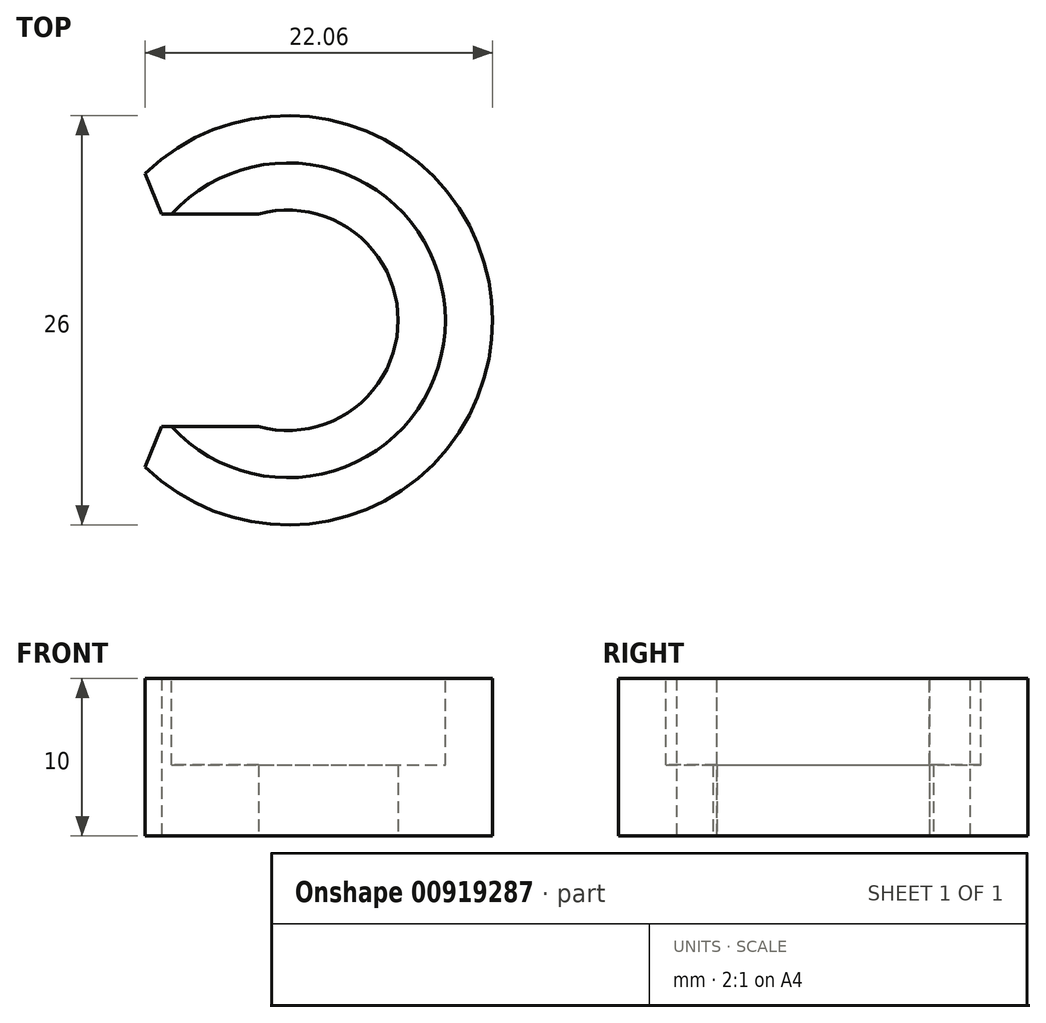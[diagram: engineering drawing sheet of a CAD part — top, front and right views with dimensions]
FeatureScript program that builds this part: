
annotation { "Feature Type Name" : "Feature", "Feature Type Description" : "" }
export const myFeature = defineFeature(function(context is Context, id is Id, definition is map)
    precondition{}
    {
        {
            var Q0;
            Q0=qCreatedBy(makeId("Top.planeOp"),FACE);
            var sketch = newSketch(context, id + "F0", { "sketchPlane" : qUnion([Q0])});
            skCircle(sketch, "E0", {"center": v(0, 0) * mm, "radius": 13 * mm});
            skCircle(sketch, "E1", {"center": v(0, 0) * mm, "radius": 7 * mm});
            skSolve(sketch);
        }
        {
            var Q0;
            Q0 = qSketchRegion(id + "F0", true);
            extrude(context, id + "F1", {"entities" : qUnion([Q0]), "depth" : 10 * mm, "offsetDistance" : 25 * mm});
        }
        {
            var Q0;
            Q0=makeQuery(id+"F1.opExtrude","CAP_FACE",FACE,{"disambiguationData":[OSD([sQuery(id+"F0.wireOp",EDGE,"E0"),sQuery(id+"F0.wireOp",EDGE,"E1")])],"isStart":false});
            var sketch = newSketch(context, id + "F2", { "sketchPlane" : qUnion([Q0])});
            skCircle(sketch, "E2", {"center": v(0, 0) * mm, "radius": 10 * mm});
            skSolve(sketch);
        }
        {
            var Q0;
            Q0=makeQuery(id+"F2.imprint","IMPRINT",FACE,{"disambiguationData":[TD([[makeQuery(id+"F2.imprint","IMPRINT",EDGE,{"derivedFrom":sQuery(id+"F2.wireOp",EDGE,"E2")}),1.0]])]});
            extrude(context, id + "F3", {"entities" : qUnion([Q0]), "operationType" : NewBodyOperationType.REMOVE, "oppositeDirection" : true, "depth" : 5.5 * mm, "offsetDistance" : 25 * mm});
        }
        {
            var Q0;
            Q0=makeQuery(id+"F1.opExtrude","CAP_FACE",FACE,{"disambiguationData":[OSD([sQuery(id+"F0.wireOp",EDGE,"E0"),sQuery(id+"F0.wireOp",EDGE,"E1")])],"isStart":false});
            var sketch = newSketch(context, id + "F4", { "sketchPlane" : qUnion([Q0])});
            skLineSegment(sketch, "E3.bottom", {"start": v(0, 6.75) * mm, "end": v(-13.5, 6.75) * mm});
            skLineSegment(sketch, "E3.top", {"start": v(0, -6.75) * mm, "end": v(-13.5, -6.75) * mm});
            skLineSegment(sketch, "E3.left", {"start": v(0, 6.75) * mm, "end": v(0, -6.75) * mm});
            skLineSegment(sketch, "E3.right", {"start": v(-13.5, 6.75) * mm, "end": v(-13.5, -6.75) * mm});
            skSolve(sketch);
        }
        {
            var Q0;
            Q0 = qSketchRegion(id + "F4", true);
            extrude(context, id + "F5", {"entities" : qUnion([Q0]), "operationType" : NewBodyOperationType.REMOVE, "endBound" : BoundingType.THROUGH_ALL, "oppositeDirection" : true, "depth" : 25 * mm, "offsetDistance" : 25 * mm});
        }
        {
            var Q0;
            Q0=makeQuery(id+"F5.boolean.opBoolean","INTERSECT",EDGE,{"derivedFrom":[makeQuery(id+"F1.opExtrude","SWEPT_FACE",FACE,{"disambiguationData":[OSD([sQuery(id+"F0.wireOp",EDGE,"E0")])]}),makeQuery(id+"F5.opExtrude","SWEPT_FACE",FACE,{"disambiguationData":[OSD([sQuery(id+"F4.wireOp",EDGE,"E3.bottom")])]})]});
            var Q1;
            Q1=makeQuery(id+"F5.boolean.opBoolean","INTERSECT",EDGE,{"derivedFrom":[makeQuery(id+"F1.opExtrude","SWEPT_FACE",FACE,{"disambiguationData":[OSD([sQuery(id+"F0.wireOp",EDGE,"E0")])]}),makeQuery(id+"F5.opExtrude","SWEPT_FACE",FACE,{"disambiguationData":[OSD([sQuery(id+"F4.wireOp",EDGE,"E3.top")])]})]});
            chamfer(context, id + "F6", {"entities" : qUnion([Q0, Q1]), "width" : 1.5 * mm, "tangentPropagation" : true});
        }
    });
